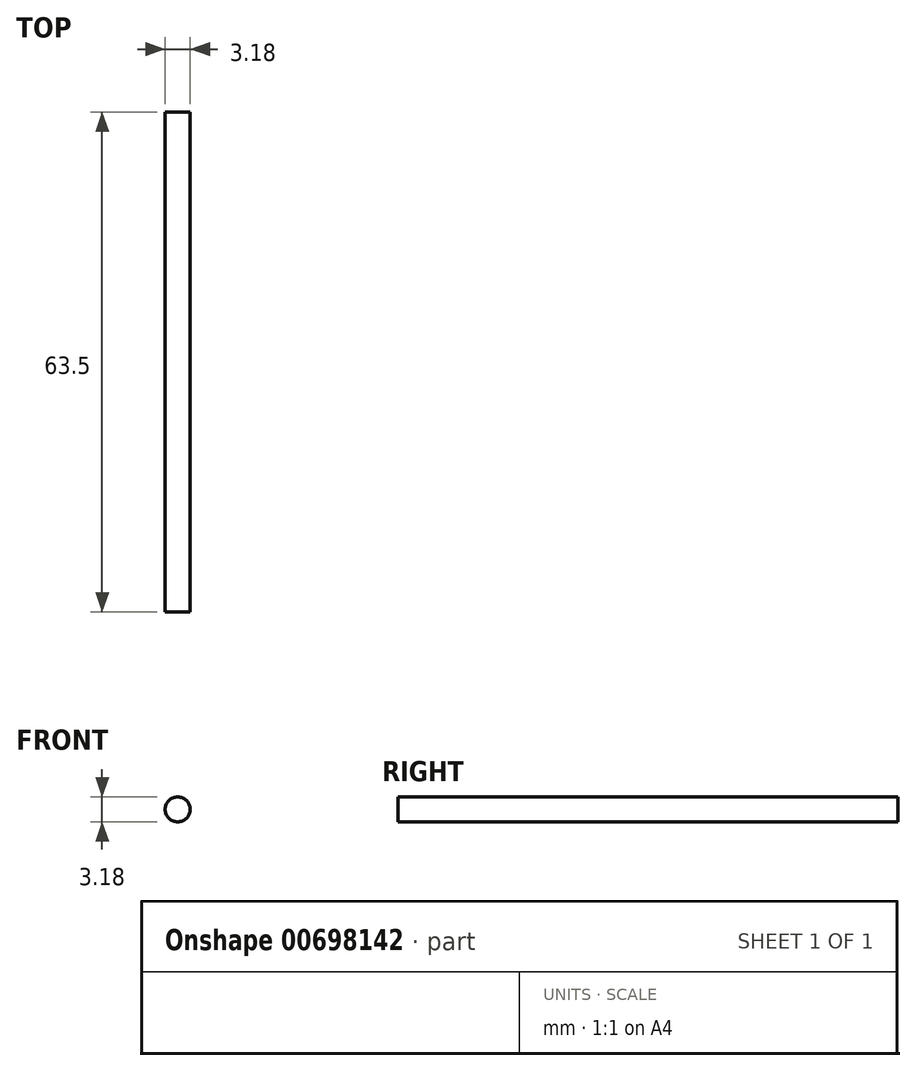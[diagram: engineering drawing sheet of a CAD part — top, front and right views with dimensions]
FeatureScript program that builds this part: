
annotation { "Feature Type Name" : "Feature", "Feature Type Description" : "" }
export const myFeature = defineFeature(function(context is Context, id is Id, definition is map)
    precondition{}
    {
        {
            var Q0;
            Q0=qCreatedBy(makeId("Front.planeOp"),FACE);
            var sketch = newSketch(context, id + "F0", { "sketchPlane" : qUnion([Q0])});
            skCircle(sketch, "E0", {"center": v(0, 0) * mm, "radius": 1.59 * mm});
            skSolve(sketch);
        }
        {
            var Q0;
            Q0=makeQuery(id+"F0.imprint","IMPRINT",FACE,{"disambiguationData":[TD([[makeQuery(id+"F0.imprint","IMPRINT",EDGE,{"derivedFrom":sQuery(id+"F0.wireOp",EDGE,"E0")}),1.0]])]});
            extrude(context, id + "F1", {"entities" : qUnion([Q0]), "depth" : 63.5 * mm, "offsetDistance" : 25.4 * mm});
        }
    });
